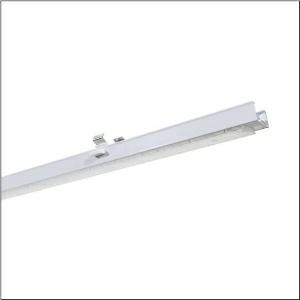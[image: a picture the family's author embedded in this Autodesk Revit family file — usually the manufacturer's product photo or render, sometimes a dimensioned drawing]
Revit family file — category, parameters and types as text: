
# Revit family: sanierungs-leuchteneinsatz_31_gen_2_51re12ma66b_cde4
name_source: partatom
category: Lighting Fixtures
units: mm (PartAtom-declared; Revit-internal decimal feet)

## family parameters
Cut with Voids When Loaded = No
Host = Face
Light Source = No
Part Type = Normal
Room Calculation Point = No
Round Connector Dimension = Use Diameter
Shared = No

## types (1)
- --- (1 x LED, 6400 lm, 40 W, 6500K)
    Apparent Load = 40 VA
    CIE Flux Codes = 65 91 98 99 100
    Color Rendering = 80
    Color Temperature = 6500K
    Default Elevation = 1800 mm
    Description = Refurbishment luminaire insert Gen.2, luminaire insert, of extruded aluminium section, coated, traffic white (RAL 9016), length: 1.172mm, width: 91mm, height: 53mm, LED rated luminous flux: 6.400lm, light colour: 865, control gear: ON/OFF Multilumen, control gear: ECG Multilumen, with system connector: socket, mains connection: 220..240V, AC/DC, 0/50..60Hz, luminous flux adjustable on luminaire in four steps (3420/4540/5580/6630lm), connected load according to luminous flux setting (20/26/33/40W), primary light control with lens, of plastic, primary optical cover: cover, of PMMA, light emission: direct distribution, protection rating (complete): IP20, insulation class (complete): insulation class I (protective earthing), certification: CE, UKCA, permissible ambient temperature for indoor applications: -20..+40°C, packaging unit: 1 piece
    Height = 58 mm
    Lamp = 1 x LED
    Lamp Light Flux = 6400 lm
    Lamp Power = 40 W
    Lamp count = 1
    Length = 1172 mm
    Luminous efficacy = 160 lm/W
    Manufacturer = Siteco
    ModVariant = No
    Model = 51RE12MA66B
    Mounting Place = Ceiling
    Mounting Type = Pendant
    Number of Poles = 1
    OnlyDefault = Yes
    Power Factor = 1
    Product Name = Sanierungs-Leuchteneinsatz 31 Gen.2
    Product group = luminaire insert
    ProductGroupID = 902
    Protection Class = Protection class I
    Protection Degree = IP 20
    RLX_Detail_Level = 1
    RlxData = <blob elided: 19933 chars, md5=a03f514a>
    Socket = socket
    Standby Power = 0 W
    System Light Flux = 6400 lm
    System Power = 40 W
    Type Comments = factory setting: luminous flux: 100 % | (ON | ON) | 300 mA
    Type Image = l_1266702.jpg
    URL = http://relux.com
    VarID = @adj_090917
    Voltage = 0 V
    Weight = 0.00 kg
    Width = 65 mm

## geometry (parser evidence)
native form markers: Blend x4, Sweep x9
no freeform markers — native parametric forms only
